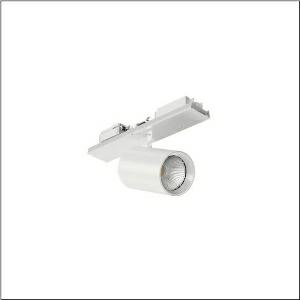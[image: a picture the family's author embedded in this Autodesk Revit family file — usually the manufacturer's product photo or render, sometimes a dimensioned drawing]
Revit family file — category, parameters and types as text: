
# Revit family: licross_r__spot_31_51sl13da43b_6d5a
name_source: partatom
category: Lighting Fixtures
units: mm (PartAtom-declared; Revit-internal decimal feet)

## family parameters
Cut with Voids When Loaded = No
Host = Face
Light Source = No
Part Type = Normal
Room Calculation Point = No
Round Connector Dimension = Use Diameter
Shared = No

## types (1)
- --- (1 x LED, 3680 lm, 28.6 W, 4000K)
    Apparent Load = 29 VA
    CIE Flux Codes = 92 97 99 100 100
    Color Rendering = 90
    Color Temperature = 4000K
    Default Elevation = 1800 mm
    Description = Licross® Spot 31, directional spotlight, light control with lens, of plastic, LED rated luminous flux: 3.680lm, light colour: 940, with plug, 5-pole, mains connection: 220..240V, AC, 50/60Hz, of aluminium, traffic white (RAL 9016), length: 300mm, diameter: 90mm, protection rating (complete): IP20, insulation class (complete): insulation class I (protective earthing), certification: CE, packaging unit: 1 piece
    Height = 175 mm
    Lamp = 1 x LED
    Lamp Light Flux = 3680 lm
    Lamp Power = 28.6 W
    Lamp count = 1
    Length = 90 mm
    Luminous efficacy = 129 lm/W
    Manufacturer = Siteco
    ModVariant = No
    Model = 51SL13DA43B
    Mounting Place = Ceiling
    Mounting Type = Pendant
    Number of Poles = 1
    OnlyDefault = Yes
    Power Factor = 1
    Product Name = Licross® Spot 31
    Product group = directional spotlight
    ProductGroupID = 906
    Protection Class = Protection class I
    Protection Degree = IP 20
    RLX_Detail_Level = 1
    RLX_Emergency_Light_Flux = 0 lm
    RLX_Emergency_Type = 0
    RLX_Emergency_Type_DB = No
    RlxData = <blob elided: 14789 chars, md5=4e0a43e0>
    Socket = socket
    Standby Power = 0 W
    System Light Flux = 3680 lm
    System Power = 29 W
    Type Comments = factory setting: luminous flux: 100 % | (ON | ON | ON) | 700 mA
    Type Image = l_1245720.jpg
    URL = http://relux.com
    VarID = @adj_132232
    Voltage = 0 V
    Weight = 0.00 kg
    Width = 0 mm  [stored 0 ft]

note: [stored X ft] marks values corroborated as IEEE doubles in the binary element streams (Revit-internal decimal feet)

## geometry (parser evidence)
native form markers: Sweep x12
no freeform markers — native parametric forms only
